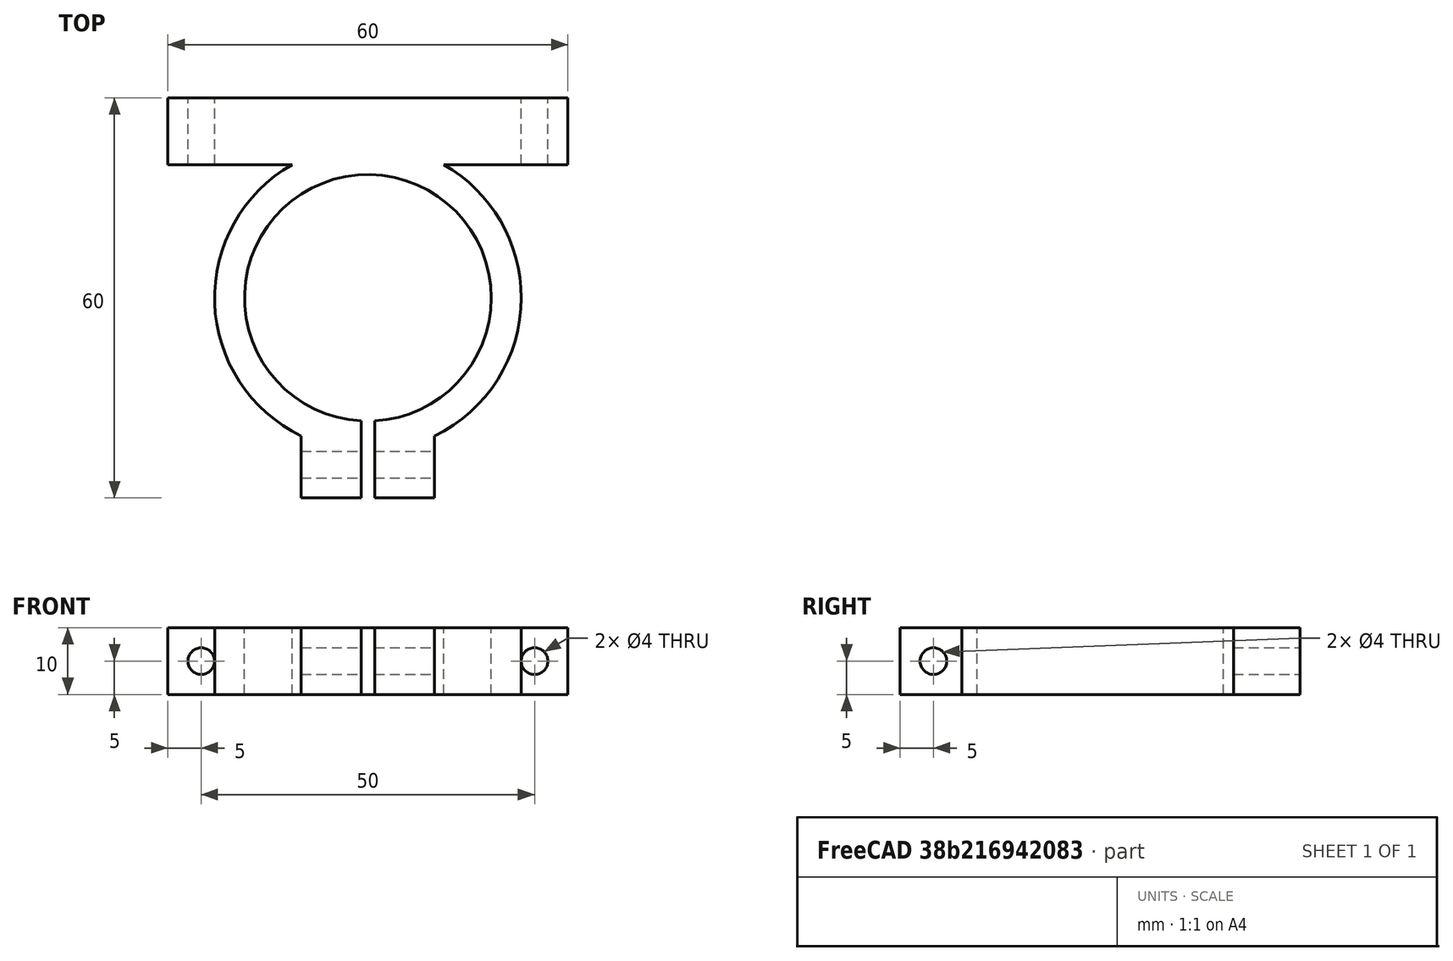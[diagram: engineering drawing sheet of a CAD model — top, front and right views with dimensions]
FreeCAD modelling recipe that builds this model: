
FCSTD DOCUMENT  (FreeCAD 0.18R16110 (Git))
Label: MotorAttachment
License: All rights reserved
LicenseURL: http://en.wikipedia.org/wiki/All_rights_reserved
objects: Part::Cylinder×5, Part::Box×3, Part::MultiFuse×2, Part::Cut×1
note: 11 computed .brp shape members not serialized (recipe doc carries the construction recipe); baked Part::Feature solids carry a one-line shape summary decoded from their .brp

FEATURE [Part::Cylinder] Cylinder
  Angle = 360
  AttacherType = Attacher::AttachEngine3D
  Height = 10
  Placement = pos=(0,0,-5) rot=(0,0,1;0rad)
  Radius = 23
FEATURE [Part::Cylinder] Cylinder001
  Angle = 360
  AttacherType = Attacher::AttachEngine3D
  Height = 10
  Placement = pos=(0,0,-5) rot=(0,0,1;0rad)
  Radius = 18.5
FEATURE [Part::Box] Box  label="Cube"
  AttacherType = Attacher::AttachEngine3D
  Height = 10
  Length = 60
  Placement = pos=(-30,20,-5) rot=(0,0,1;0rad)
  Width = 10
FEATURE [Part::Cylinder] Cylinder002
  Angle = 360
  AttacherType = Attacher::AttachEngine3D
  Height = 10
  Placement = pos=(25,20,-4e-15) rot=(-1,0,0;1.5708rad)
  Radius = 2
FEATURE [Part::Cylinder] Cylinder003
  Angle = 360
  AttacherType = Attacher::AttachEngine3D
  Height = 10
  Placement = pos=(-25,20,-4e-15) rot=(-1,0,0;1.5708rad)
  Radius = 2
FEATURE [Part::Box] Box001  label="Cube001"
  AttacherType = Attacher::AttachEngine3D
  Height = 10
  Length = 20
  Placement = pos=(-10,-30,-5) rot=(0,0,1;0rad)
  Width = 10
FEATURE [Part::MultiFuse] Fusion  label="Positive Fusion"
  Shapes = -> [Cylinder,Box,Box001]
FEATURE [Part::Cylinder] Cylinder004
  Angle = 360
  AttacherType = Attacher::AttachEngine3D
  Height = 20
  Placement = pos=(-10,-25,-2.2e-15) rot=(0,1,0;1.5708rad)
  Radius = 2
FEATURE [Part::Box] Box002  label="Cube002"
  AttacherType = Attacher::AttachEngine3D
  Height = 10
  Length = 2
  Placement = pos=(-1,-30,-5) rot=(0,0,1;0rad)
  Width = 15
FEATURE [Part::MultiFuse] Fusion001  label="Negative Fusion"
  Shapes = -> [Cylinder003,Cylinder002,Cylinder001,Cylinder004,Box002]
FEATURE [Part::Cut] Cut
  Base = -> Fusion
  Tool = -> Fusion001
